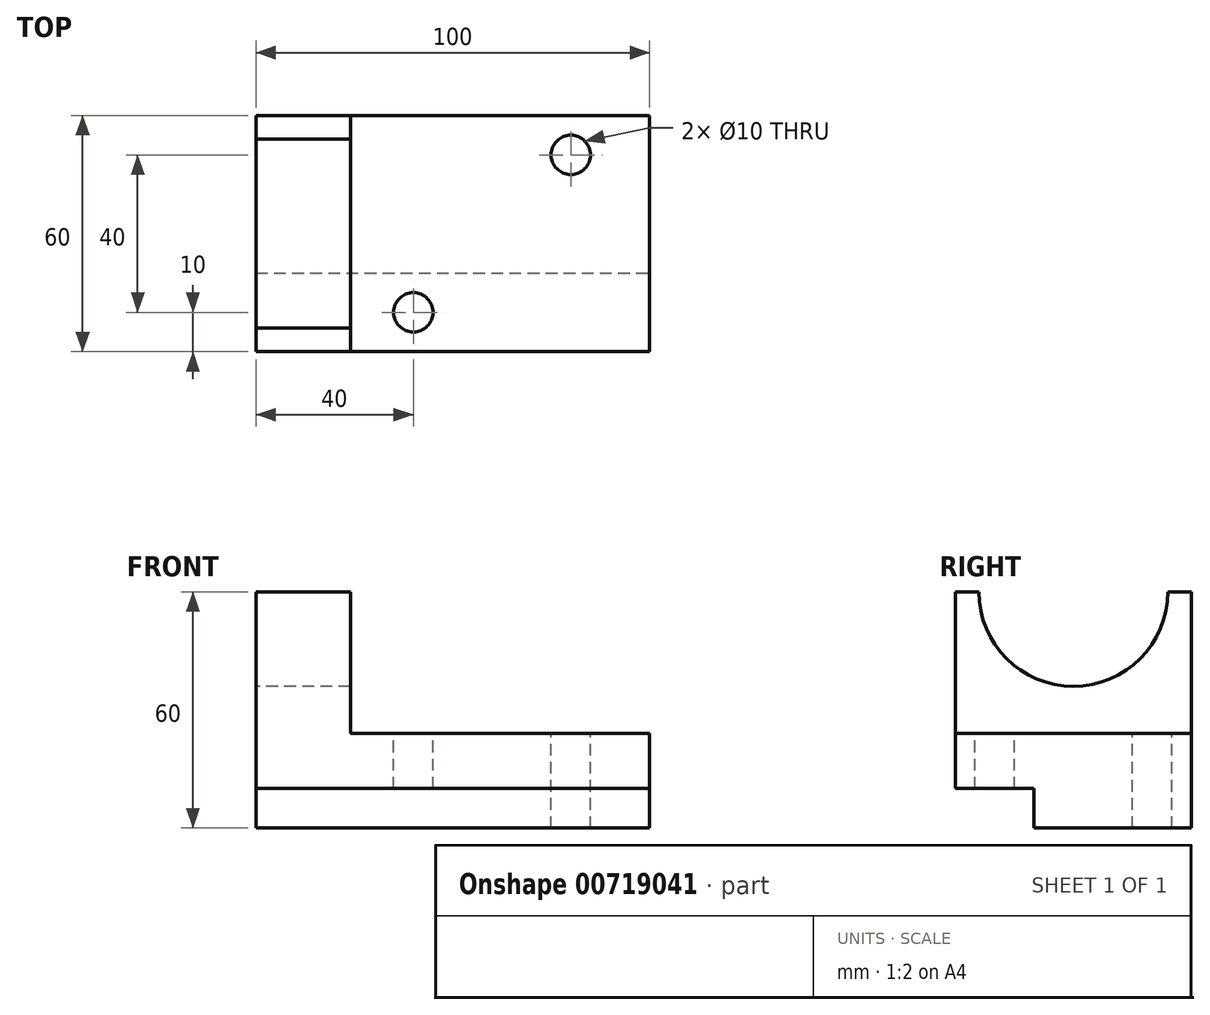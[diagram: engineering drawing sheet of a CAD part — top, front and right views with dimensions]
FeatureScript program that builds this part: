
annotation { "Feature Type Name" : "Feature", "Feature Type Description" : "" }
export const myFeature = defineFeature(function(context is Context, id is Id, definition is map)
    precondition{}
    {
        {
            var Q0;
            Q0=qCreatedBy(makeId("Right.planeOp"),FACE);
            var sketch = newSketch(context, id + "F0", { "sketchPlane" : qUnion([Q0])});
            skLineSegment(sketch, "E0", {"start": v(0, -10) * mm, "end": v(0, 14) * mm});
            skLineSegment(sketch, "E1", {"start": v(0, 14) * mm, "end": v(-60, 14) * mm});
            skLineSegment(sketch, "E2", {"start": v(-60, 14) * mm, "end": v(-60, 0) * mm});
            skLineSegment(sketch, "E3", {"start": v(-60, 0) * mm, "end": v(-40, 0) * mm});
            skLineSegment(sketch, "E4", {"start": v(-40, 0) * mm, "end": v(-40, -10) * mm});
            skLineSegment(sketch, "E5", {"start": v(-40, -10) * mm, "end": v(0, -10) * mm});
            skSolve(sketch);
        }
        {
            var Q0;
            Q0=makeQuery(id+"F0.imprint","IMPRINT",FACE,{"disambiguationData":[TD([[makeQuery(id+"F0.imprint","IMPRINT",EDGE,{"derivedFrom":sQuery(id+"F0.wireOp",EDGE,"E0")}),1.0]])]});
            extrude(context, id + "F1", {"entities" : qUnion([Q0]), "oppositeDirection" : true, "depth" : 100 * mm, "offsetDistance" : 25 * mm});
        }
        {
            var Q0;
            Q0=makeQuery(id+"F1.opExtrude","CAP_FACE",FACE,{"disambiguationData":[OSD([sQuery(id+"F0.wireOp",EDGE,"E0"),sQuery(id+"F0.wireOp",EDGE,"E1"),sQuery(id+"F0.wireOp",EDGE,"E2"),sQuery(id+"F0.wireOp",EDGE,"E3"),sQuery(id+"F0.wireOp",EDGE,"E4"),sQuery(id+"F0.wireOp",EDGE,"E5")])],"isStart":false});
            var sketch = newSketch(context, id + "F2", { "sketchPlane" : qUnion([Q0])});
            skLineSegment(sketch, "E6.bottom", {"start": v(0, 14) * mm, "end": v(60, 14) * mm});
            skLineSegment(sketch, "E6.top", {"start": v(0, 50) * mm, "end": v(6, 50) * mm});
            skLineSegment(sketch, "E6.left", {"start": v(0, 14) * mm, "end": v(0, 50) * mm});
            skLineSegment(sketch, "E6.right", {"start": v(60, 14) * mm, "end": v(60, 50) * mm});
            skArc(sketch, "E7", {"start": v(6, 50) * mm, "mid": v(30, 26) * mm, "end": v(54, 50) * mm});
            skLineSegment(sketch, "E8.trimOffspring", {"start": v(54, 50) * mm, "end": v(60, 50) * mm});
            skSolve(sketch);
        }
        {
            var Q0;
            Q0=makeQuery(id+"F2.imprint","IMPRINT",FACE,{"disambiguationData":[TD([[makeQuery(id+"F2.imprint","IMPRINT",EDGE,{"derivedFrom":sQuery(id+"F2.wireOp",EDGE,"E6.bottom")}),1.0]])]});
            extrude(context, id + "F3", {"entities" : qUnion([Q0]), "operationType" : NewBodyOperationType.ADD, "oppositeDirection" : true, "depth" : 24 * mm, "offsetDistance" : 25 * mm});
        }
        {
            var Q0;
            Q0=makeQuery(id+"F1.opExtrude","SWEPT_FACE",FACE,{"disambiguationData":[OSD([sQuery(id+"F0.wireOp",EDGE,"E1")])]});
            var sketch = newSketch(context, id + "F4", { "sketchPlane" : qUnion([Q0])});
            skCircle(sketch, "E9", {"center": v(-20, -10) * mm, "radius": 5 * mm});
            skCircle(sketch, "E10", {"center": v(-60, -50) * mm, "radius": 5 * mm});
            skSolve(sketch);
        }
        {
            var Q0;
            Q0=makeQuery(id+"F4.imprint","IMPRINT",FACE,{"disambiguationData":[TD([[makeQuery(id+"F4.imprint","IMPRINT",EDGE,{"derivedFrom":sQuery(id+"F4.wireOp",EDGE,"E9")}),1.0]])]});
            var Q1;
            Q1=makeQuery(id+"F4.imprint","IMPRINT",FACE,{"disambiguationData":[TD([[makeQuery(id+"F4.imprint","IMPRINT",EDGE,{"derivedFrom":sQuery(id+"F4.wireOp",EDGE,"E10")}),1.0]])]});
            extrude(context, id + "F5", {"entities" : qUnion([Q0, Q1]), "operationType" : NewBodyOperationType.REMOVE, "oppositeDirection" : true, "depth" : 25 * mm, "offsetDistance" : 25 * mm});
        }
    });
